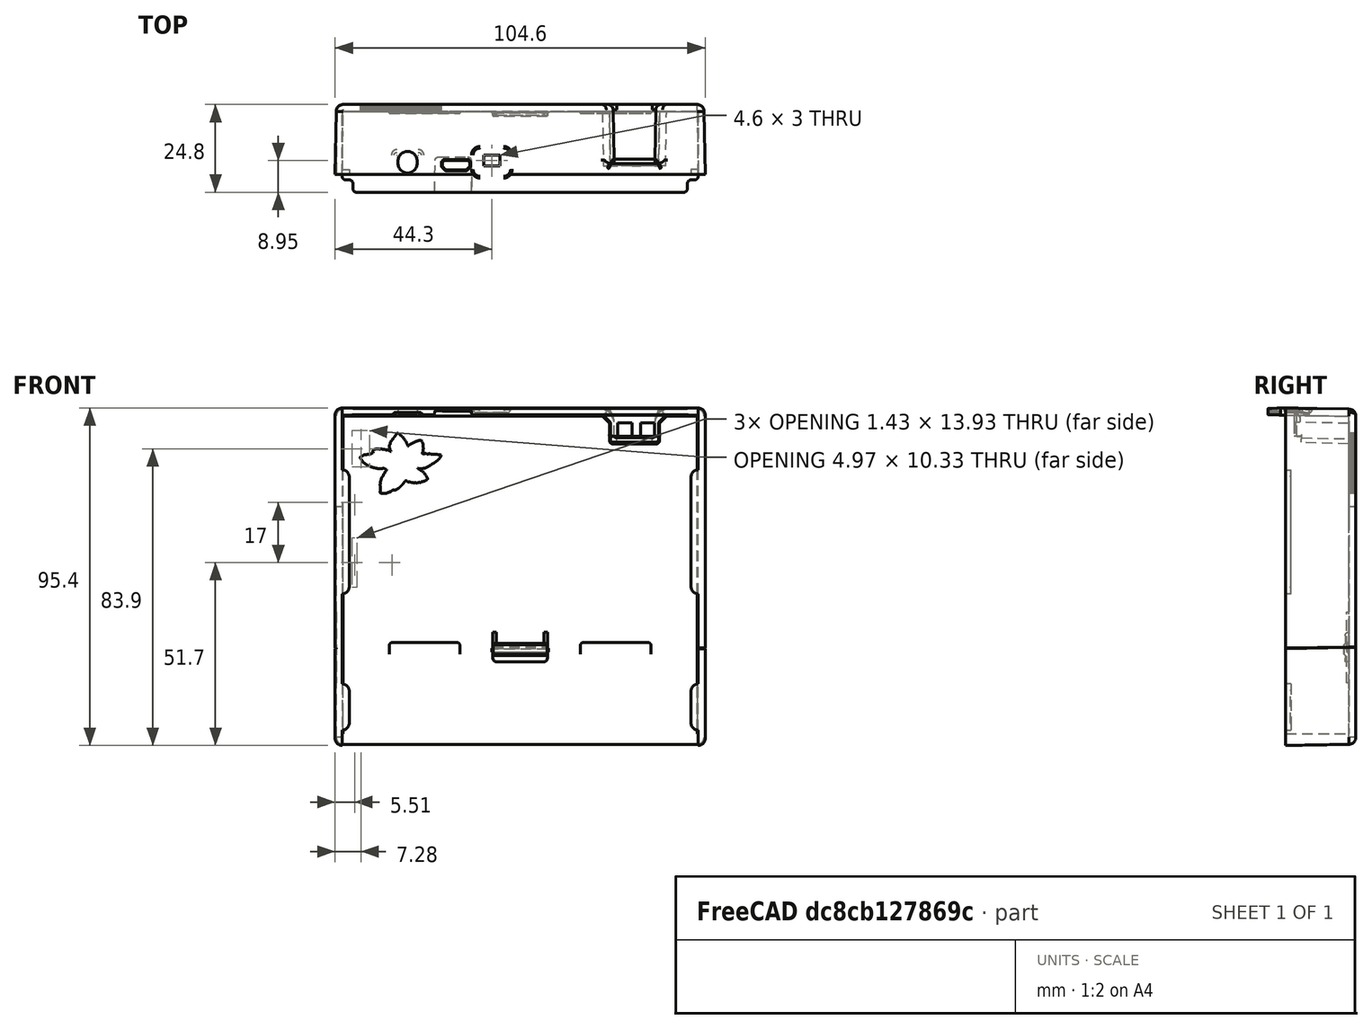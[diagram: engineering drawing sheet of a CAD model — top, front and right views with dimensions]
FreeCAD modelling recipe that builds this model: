
FCSTD DOCUMENT  (FreeCAD 0.20R29410 (Git))
Label: N2CaseOnePeice_10_18_2022
License: All rights reserved
LicenseURL: http://en.wikipedia.org/wiki/All_rights_reserved
objects: Part::Box×5, Part::Feature×3, Part::Cut×3, Part::MultiFuse×2, Mesh::Feature×1, Part::Cylinder×1
note: 14 computed .brp shape members not serialized (recipe doc carries the construction recipe); baked Part::Feature solids carry a one-line shape summary decoded from their .brp

FEATURE [Part::Feature] Solid  label="N2_BOTTOM_COVER"
  shape: bbox 104.6 x 25.21 x 71.78 mm, 343 faces (baked)
FEATURE [Part::Feature] Solid001  label="N2_TOP_COVER"
  shape: bbox 104.6 x 24.81 x 29.22 mm, 349 faces (baked)
FEATURE [Part::Box] Box  label="Cube"
  AttacherType = Attacher::AttachEngine3D
  Height = 15
  Length = 62.5
  Placement = pos=(-49,18,44) rot=(0,1,0;1.5708rad)
  Width = 2
FEATURE [Part::MultiFuse] Fusion  label="BottomCover"
  Shapes = -> [Solid,Box]
FEATURE [Part::Box] Box001  label="Cube001"
  AttacherType = Attacher::AttachEngine3D
  Height = 15
  Length = 97.5
  Placement = pos=(48.5,20,-3.5) rot=(0,1,0;3.14159rad)
  Width = 2
FEATURE [Part::Cut] Cut
  Base = -> Fusion
  Tool = -> Box001
FEATURE [Part::Box] Box021  label="Cube009"
  AttacherType = Attacher::AttachEngine3D
  Height = 32.5
  Length = 97.5
  Placement = pos=(48.5,18,-11.9) rot=(0,1,0;3.14159rad)
  Width = 2
FEATURE [Part::Box] Box070  label="Cube010"
  AttacherType = Attacher::AttachEngine3D
  Height = 20
  Length = 1.7
  Placement = pos=(-50.3,0.2,-10) rot=(0,1,0;3.14159rad)
  Width = 17.8
FEATURE [Part::Box] Box071  label="cuts001"
  AttacherType = Attacher::AttachEngine3D
  Height = 10
  Length = 23
  Placement = pos=(50.3,-5,-54.4) rot=(0,0,1;1.5708rad)
  Width = 100.6
FEATURE [Mesh::Feature] _9G1ElevatedDesign  label="99G1ElevatedDesign"
  Placement = pos=(-31.68,17.29,30.95) rot=(1,0,0;4.71239rad)
FEATURE [Part::Cylinder] Cylinder011
  Angle = 90
  AttacherType = Attacher::AttachEngine3D
  FirstAngle = 0
  Height = 65.2
  Placement = pos=(-50,18,-45.4) rot=(0,0,1;1.5708rad)
  Radius = 2
  SecondAngle = 0
FEATURE [Part::MultiFuse] Fusion001
  Shapes = -> [Solid001,Cut,Box021,Cylinder011,Box070]
FEATURE [Part::Cut] Cut001
  Base = -> Fusion001
  Tool = -> Box071
FEATURE [Part::Feature] Part__Feature060  label="logoTopCut"
  Placement = pos=(-65,23.8,47) rot=(-1,0,0;3.14159rad)
  shape: bbox 22.79 x 8 x 17.08 mm, 886 faces (baked)
FEATURE [Part::Cut] Cut002
  Base = -> Cut001
  Tool = -> Part__Feature060
